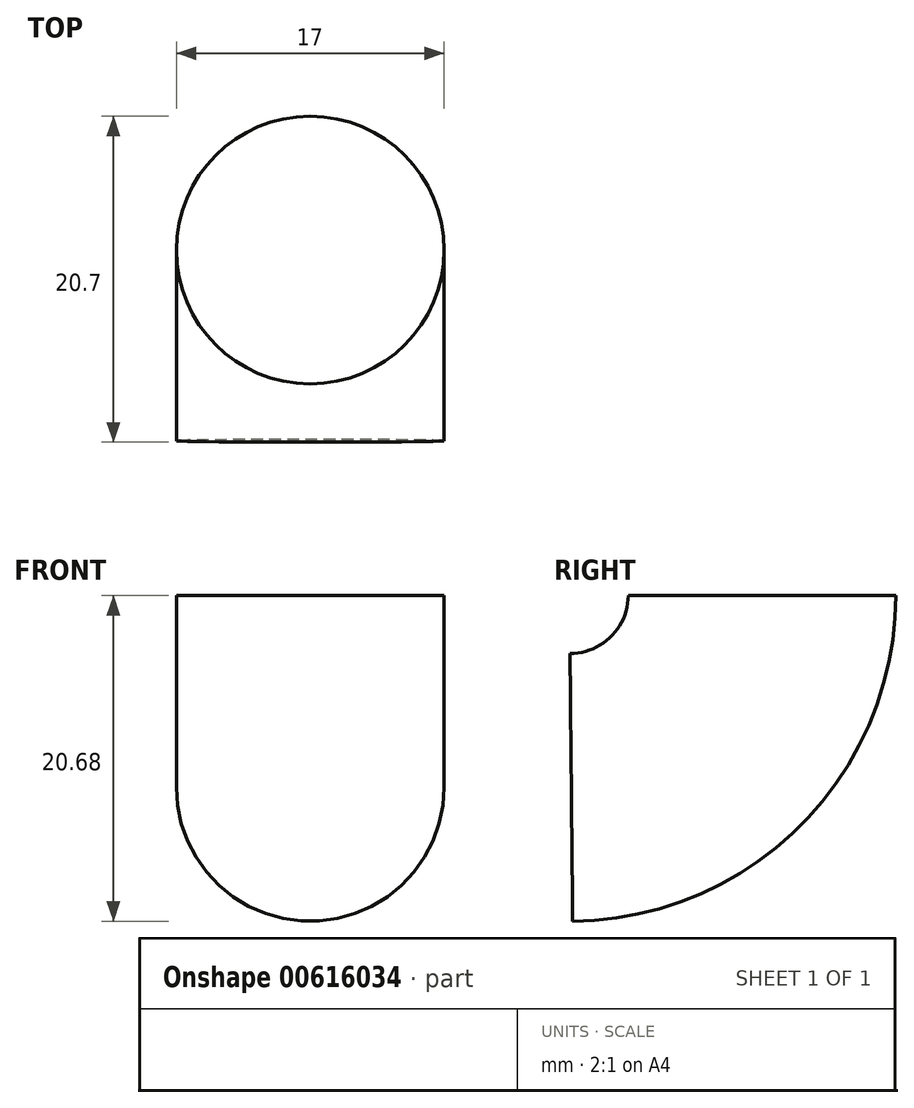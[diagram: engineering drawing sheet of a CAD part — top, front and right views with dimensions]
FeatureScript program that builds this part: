
annotation { "Feature Type Name" : "Feature", "Feature Type Description" : "" }
export const myFeature = defineFeature(function(context is Context, id is Id, definition is map)
    precondition{}
    {
        {
            var Q0;
            Q0=qCreatedBy(makeId("Top.planeOp"),FACE);
            var sketch = newSketch(context, id + "F0", { "sketchPlane" : qUnion([Q0])});
            skCircle(sketch, "E0", {"center": v(0, 0) * mm, "radius": 8.5 * mm});
            skSolve(sketch);
        }
        {
            var Q0;
            Q0=qCreatedBy(makeId("Right.planeOp"),FACE);
            var sketch = newSketch(context, id + "F1", { "sketchPlane" : qUnion([Q0])});
            skEllipse(sketch, "E1", {"center": v(-12.02, 0) * mm, "majorRadius": 12.02 * mm, "minorRadius": 12.16 * mm, "majorAxis": v(1, 0)});
            skSolve(sketch);
        }
        {
            var Q0;
            Q0=makeQuery(id+"F1.imprint","IMPRINT",FACE,{"disambiguationData":[TD([[makeQuery(id+"F1.imprint","IMPRINT",EDGE,{"derivedFrom":sQuery(id+"F1.wireOp",EDGE,"E1")}),1.0]])]});
            var sketch = newSketch(context, id + "F2", { "sketchPlane" : qUnion([Q0])});
            skArc(sketch, "E2", {"start": v(-12.11, -12.18) * mm, "mid": v(-3.55, -8.58) * mm, "end": v(0, 0) * mm});
            skSolve(sketch);
        }
        {
            var Q0;
            Q0=makeQuery(id+"F0.imprint","IMPRINT",FACE,{"disambiguationData":[TD([[makeQuery(id+"F0.imprint","IMPRINT",EDGE,{"derivedFrom":sQuery(id+"F0.wireOp",EDGE,"E0")}),1.0]])]});
            var Q1;
            Q1 = qConstructionFilter(qBodyType(qCreatedBy(id + "F2" ,EDGE), BodyType.WIRE), ConstructionObject.NO);
            sweep(context, id + "F3", {"profiles" : qUnion([Q0]), "path" : qUnion([Q1])});
        }
    });
